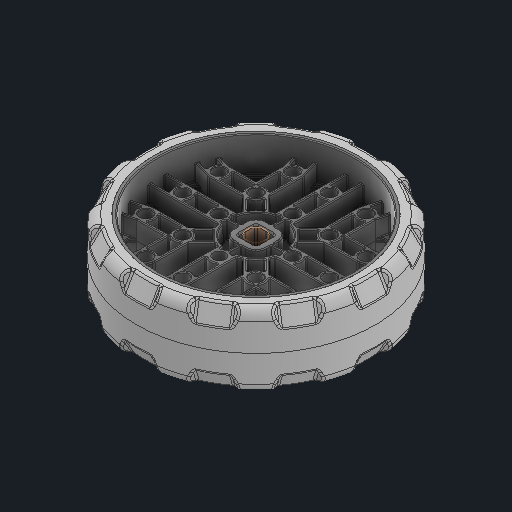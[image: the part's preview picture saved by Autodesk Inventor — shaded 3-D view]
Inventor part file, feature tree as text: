
AUTODESK INVENTOR PART (.ipt)
format: ipt  version: 2024 (Build 280153000, 153)  size: 7,959,040 bytes
history: native  units: in
note: dims shown in document units (in); Inventor stores cm internally (conversion verified against a paired STEP export)
features: other x3, extrude x1
ambient origin geometry x8: Origin, YZ Plane, XZ Plane, XY Plane, X Axis, Y Axis, Z Axis, Center Point
bodies: Solid1 (feature_tree), Solid2 (feature_tree)
feature tree (4):
  other  "Srf1"
  other  "276-7771-001 Rev4_1:1"
  other  "276-7771-002 Rev4_2:1"
  extrude  "ExtrusionSrf1"  Depth=0.3937in TaperAngle=0.0deg
